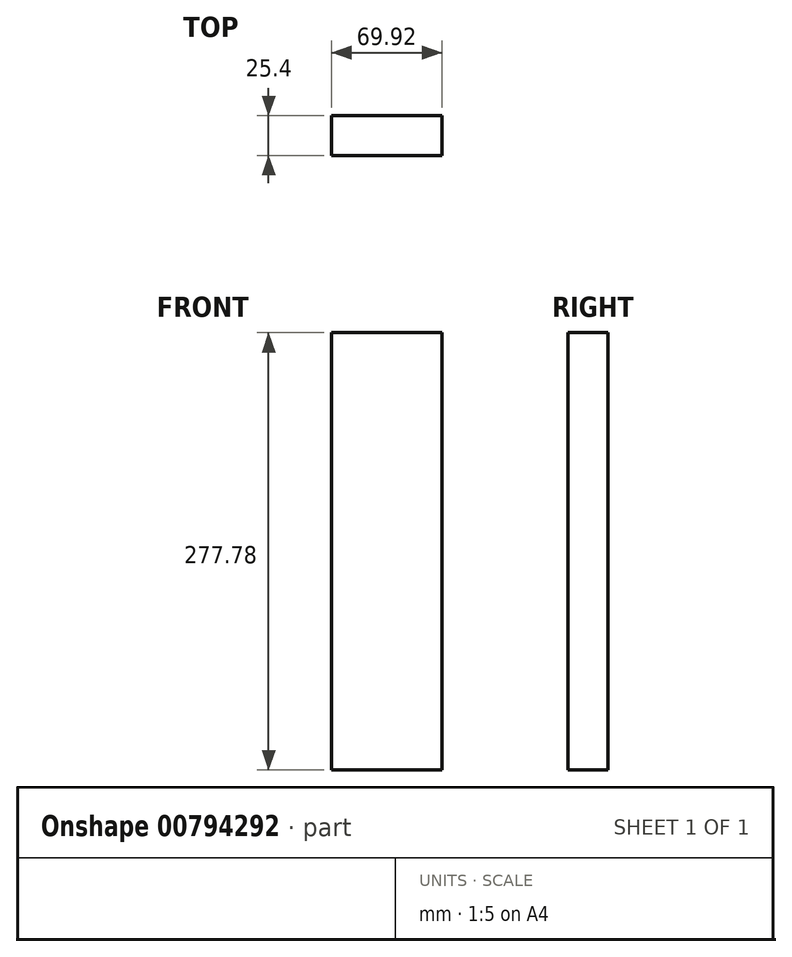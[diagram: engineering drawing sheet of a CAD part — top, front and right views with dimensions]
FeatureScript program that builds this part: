
annotation { "Feature Type Name" : "Feature", "Feature Type Description" : "" }
export const myFeature = defineFeature(function(context is Context, id is Id, definition is map)
    precondition{}
    {
        {
            var Q0;
            Q0=qCreatedBy(makeId("Front.planeOp"),FACE);
            var sketch = newSketch(context, id + "F0", { "sketchPlane" : qUnion([Q0])});
            skLineSegment(sketch, "E0.bottom", {"start": v(-34.96, 138.9) * mm, "end": v(34.96, 138.9) * mm});
            skLineSegment(sketch, "E0.top", {"start": v(-34.96, -138.9) * mm, "end": v(34.96, -138.9) * mm});
            skLineSegment(sketch, "E0.left", {"start": v(-34.96, 138.9) * mm, "end": v(-34.96, -138.9) * mm});
            skLineSegment(sketch, "E0.right", {"start": v(34.96, 138.9) * mm, "end": v(34.96, -138.9) * mm});
            skPoint(sketch, "E0.middle", {"position": v(0, 0) * mm});
            skLineSegment(sketch, "E1", {"start": v(-34.96, 40.37) * mm, "end": v(34.96, 0) * mm});
            skSolve(sketch);
        }
        {
            var Q0;
            {var subQ0=sQuery(id+"F0.wireOp",EDGE,"E0.bottom");Q0=makeQuery(id+"F0.imprint","IMPRINT",FACE,{"disambiguationData":[TD([[makeQuery(id+"F0.imprint","IMPRINT",EDGE,{"derivedFrom":subQ0}),-1.0]])]});}
            extrude(context, id + "F1", {"entities" : qUnion([Q0]), "depth" : 25.4 * mm, "offsetDistance" : 25.4 * mm});
        }
        {
            var Q0;
            {var subQ0=sQuery(id+"F0.wireOp",EDGE,"E0.top");Q0=makeQuery(id+"F0.imprint","IMPRINT",FACE,{"disambiguationData":[TD([[makeQuery(id+"F0.imprint","IMPRINT",EDGE,{"derivedFrom":subQ0}),1.0]])]});}
            extrude(context, id + "F2", {"entities" : qUnion([Q0]), "operationType" : NewBodyOperationType.ADD, "depth" : 25.4 * mm, "offsetDistance" : 25.4 * mm});
        }
        {
            var Q0;
            {var subQ0=sQuery(id+"F0.wireOp",EDGE,"E0.right");Q0=makeQuery(id+"F2.boolean.opBoolean","MERGE",FACE,{"derivedFrom":[makeQuery(id+"F1.opExtrude","SWEPT_FACE",FACE,{"disambiguationData":[OSD([subQ0])]}),makeQuery(id+"F2.opExtrude","SWEPT_FACE",FACE,{"disambiguationData":[OSD([subQ0])]})]});}
            var sketch = newSketch(context, id + "F3", { "sketchPlane" : qUnion([Q0])});
            skPoint(sketch, "E2.0", {"position": v(0, 40.37) * mm});
            skLineSegment(sketch, "E3", {"start": v(0, 40.37) * mm, "end": v(-25.4, 40.37) * mm});
            skLineSegment(sketch, "E4", {"start": v(0, 0) * mm, "end": v(-25.4, 0) * mm});
            skLineSegment(sketch, "E5", {"start": v(-25.4, 40.37) * mm, "end": v(-25.4, 0) * mm});
            skSolve(sketch);
        }
        {
            var Q0;
            Q0=sQuery(id+"F0.wireOp",EDGE,"E1");
            extrude(context, id + "F4", {"bodyType" : ToolBodyType.SURFACE, "surfaceEntities" : qUnion([Q0]), "endBound" : BoundingType.UP_TO_NEXT, "depth" : 25.4 * mm, "offsetDistance" : 25.4 * mm});
        }
    });
